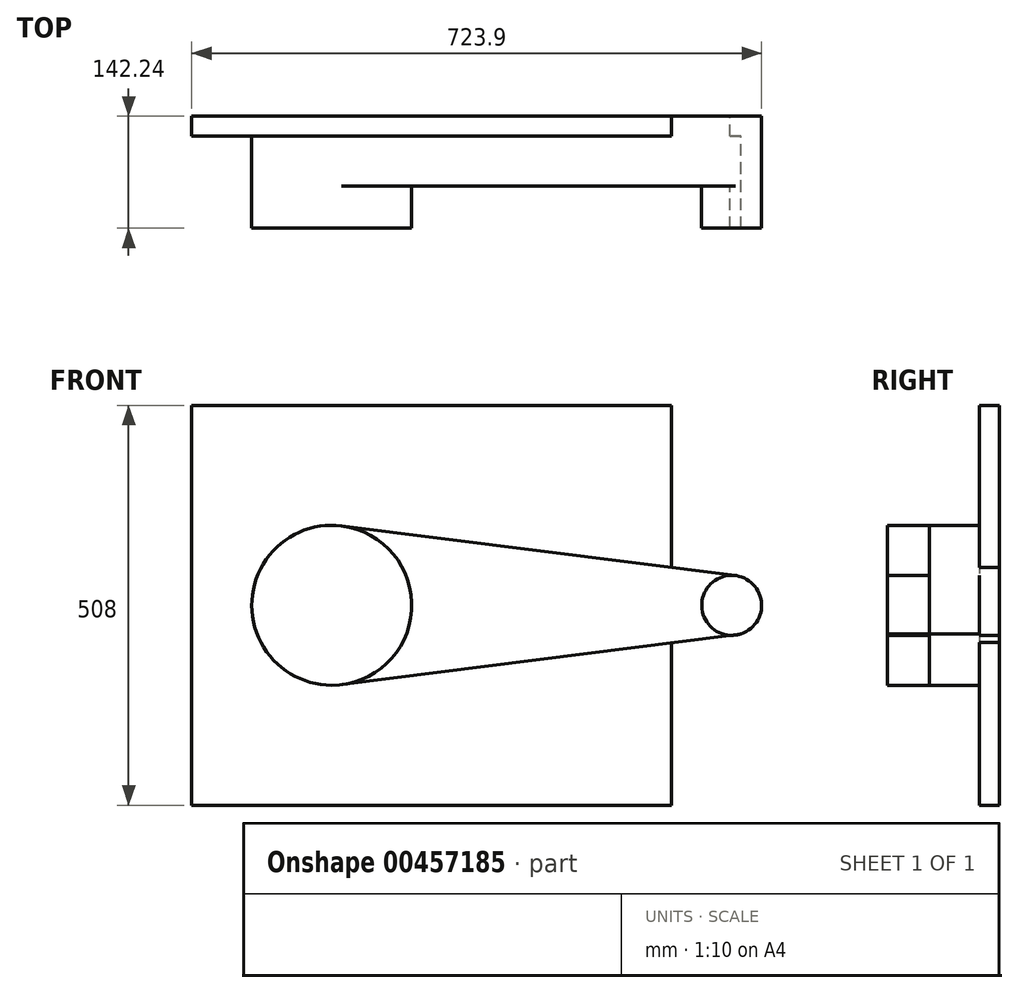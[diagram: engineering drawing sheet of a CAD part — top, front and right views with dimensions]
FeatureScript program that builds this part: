
annotation { "Feature Type Name" : "Feature", "Feature Type Description" : "" }
export const myFeature = defineFeature(function(context is Context, id is Id, definition is map)
    precondition{}
    {
        {
            var Q0;
            Q0=qCreatedBy(makeId("Front.planeOp"),FACE);
            var sketch = newSketch(context, id + "F0", { "sketchPlane" : qUnion([Q0])});
            skLineSegment(sketch, "E0.bottom", {"start": v(-381, 254) * mm, "end": v(228.6, 254) * mm});
            skLineSegment(sketch, "E0.top", {"start": v(-381, -254) * mm, "end": v(228.6, -254) * mm});
            skLineSegment(sketch, "E0.left", {"start": v(-381, 254) * mm, "end": v(-381, -254) * mm});
            skLineSegment(sketch, "E0.right", {"start": v(228.6, 254) * mm, "end": v(228.6, -254) * mm});
            skCircle(sketch, "E1", {"center": v(-203.2, 0) * mm, "radius": 101.6 * mm});
            skCircle(sketch, "E2", {"center": v(304.8, 0) * mm, "radius": 38.1 * mm});
            skLineSegment(sketch, "E3", {"start": v(-190.5, 100.8) * mm, "end": v(309.56, 37.8) * mm});
            skLineSegment(sketch, "E4", {"start": v(-190.36, -100.79) * mm, "end": v(316.61, -36.22) * mm});
            skSolve(sketch);
        }
        {
            var Q0;
            Q0 = qSketchRegion(id + "F0", true);
            var Q1;
            {var subQ0=sQuery(id+"F0.wireOp",EDGE,"E1");var subQ1=makeQuery(id+"F0.imprint","INTERSECT",VERTEX,{"derivedFrom":[subQ0,sQuery(id+"F0.wireOp",EDGE,"E3")]});Q1=makeQuery(id+"F0.imprint","IMPRINT",FACE,{"disambiguationData":[TD([[makeQuery(id+"F0.imprint","IMPRINT",EDGE,{"disambiguationData":[TD([[subQ1,-1.0]])],"derivedFrom":subQ0}),1.0]])]});}
            var Q2;
            {var subQ0=sQuery(id+"F0.wireOp",EDGE,"E3");Q2=makeQuery(id+"F0.imprint","IMPRINT",FACE,{"disambiguationData":[TD([[makeQuery(id+"F0.imprint","IMPRINT",EDGE,{"derivedFrom":subQ0}),-1.0]])]});}
            var Q3;
            {var subQ0=sQuery(id+"F0.wireOp",EDGE,"E2");var subQ1=makeQuery(id+"F0.imprint","INTERSECT",VERTEX,{"derivedFrom":[subQ0,sQuery(id+"F0.wireOp",EDGE,"E3")]});Q3=makeQuery(id+"F0.imprint","IMPRINT",FACE,{"disambiguationData":[TD([[makeQuery(id+"F0.imprint","IMPRINT",EDGE,{"disambiguationData":[TD([[subQ1,-1.0]])],"derivedFrom":subQ0}),1.0]])]});}
            extrude(context, id + "F1", {"entities" : qUnion([Q0, Q1, Q2, Q3]), "depth" : 25.4 * mm});
        }
        {
            var Q0;
            {var subQ0=sQuery(id+"F0.wireOp",EDGE,"E2");var subQ1=makeQuery(id+"F0.imprint","INTERSECT",VERTEX,{"derivedFrom":[subQ0,sQuery(id+"F0.wireOp",EDGE,"E3")]});Q0=makeQuery(id+"F0.imprint","IMPRINT",FACE,{"disambiguationData":[TD([[makeQuery(id+"F0.imprint","IMPRINT",EDGE,{"disambiguationData":[TD([[subQ1,-1.0]])],"derivedFrom":subQ0}),1.0]])]});}
            var Q1;
            {var subQ0=sQuery(id+"F0.wireOp",EDGE,"E1");var subQ1=makeQuery(id+"F0.imprint","INTERSECT",VERTEX,{"derivedFrom":[subQ0,sQuery(id+"F0.wireOp",EDGE,"E3")]});Q1=makeQuery(id+"F0.imprint","IMPRINT",FACE,{"disambiguationData":[TD([[makeQuery(id+"F0.imprint","IMPRINT",EDGE,{"disambiguationData":[TD([[subQ1,-1.0]])],"derivedFrom":subQ0}),1.0]])]});}
            var Q2;
            {var subQ0=sQuery(id+"F0.wireOp",EDGE,"E3");Q2=makeQuery(id+"F0.imprint","IMPRINT",FACE,{"disambiguationData":[TD([[makeQuery(id+"F0.imprint","IMPRINT",EDGE,{"derivedFrom":subQ0}),-1.0]])]});}
            extrude(context, id + "F2", {"entities" : qUnion([Q0, Q1, Q2]), "operationType" : NewBodyOperationType.ADD, "depth" : 88.9 * mm});
        }
        {
            var Q0;
            {var subQ0=sQuery(id+"F0.wireOp",EDGE,"E2");var subQ1=makeQuery(id+"F0.imprint","INTERSECT",VERTEX,{"derivedFrom":[subQ0,sQuery(id+"F0.wireOp",EDGE,"E3")]});Q0=makeQuery(id+"F0.imprint","IMPRINT",FACE,{"disambiguationData":[TD([[makeQuery(id+"F0.imprint","IMPRINT",EDGE,{"disambiguationData":[TD([[subQ1,-1.0]])],"derivedFrom":subQ0}),1.0]])]});}
            var Q1;
            {var subQ0=sQuery(id+"F0.wireOp",EDGE,"E1");var subQ1=makeQuery(id+"F0.imprint","INTERSECT",VERTEX,{"derivedFrom":[subQ0,sQuery(id+"F0.wireOp",EDGE,"E3")]});Q1=makeQuery(id+"F0.imprint","IMPRINT",FACE,{"disambiguationData":[TD([[makeQuery(id+"F0.imprint","IMPRINT",EDGE,{"disambiguationData":[TD([[subQ1,-1.0]])],"derivedFrom":subQ0}),1.0]])]});}
            extrude(context, id + "F3", {"entities" : qUnion([Q0, Q1]), "operationType" : NewBodyOperationType.ADD, "depth" : 142.24 * mm});
        }
    });
